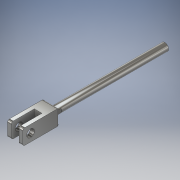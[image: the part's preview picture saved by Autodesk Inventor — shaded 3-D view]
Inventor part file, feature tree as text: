
AUTODESK INVENTOR PART (.ipt)
format: ipt  version: 2017 SP1 (Build 210196100, 196)  size: 153,088 bytes
history: native  units: in
note: dims shown in document units (in); Inventor stores cm internally (conversion verified against a paired STEP export)
features: extrude x5, sketch x5, fillet x1
ambient origin geometry x8: Origin, YZ Plane, XZ Plane, XY Plane, X Axis, Y Axis, Z Axis, Center Point
bodies: Solid1 (feature_tree)
feature tree (11):
  extrude  "Extrusion1"  Depth=3.5in TaperAngle=0.0deg
  extrude  "Extrusion2"  Depth=0.2in TaperAngle=0.0deg
  extrude  "Extrusion3"  Depth=0.44in TaperAngle=0.0deg
  extrude  "Extrusion4"  Depth=0.75in TaperAngle=0.0deg
  extrude  "Extrusion5"  Depth=0.25in
  fillet  "Fillet1"  Radius=0.75in
  sketch  "Sketch1"  dims[d0=0.25in d1=3.5in d2=0.0in]
  sketch  "Sketch2"  dims[d3=0.125in d4=0.2in d5=0.0in]
  sketch  "Sketch3"  dims[d6=0.5in d7=0.44in d8=0.0in]
  sketch  "Sketch4"  dims[d9=0.25in d10=0.75in d11=0.0in]
  sketch  "Sketch5"  dims[d12=0.25in d13=0.25in d14=0.75in d15=0.0in d16=0.0625in]
